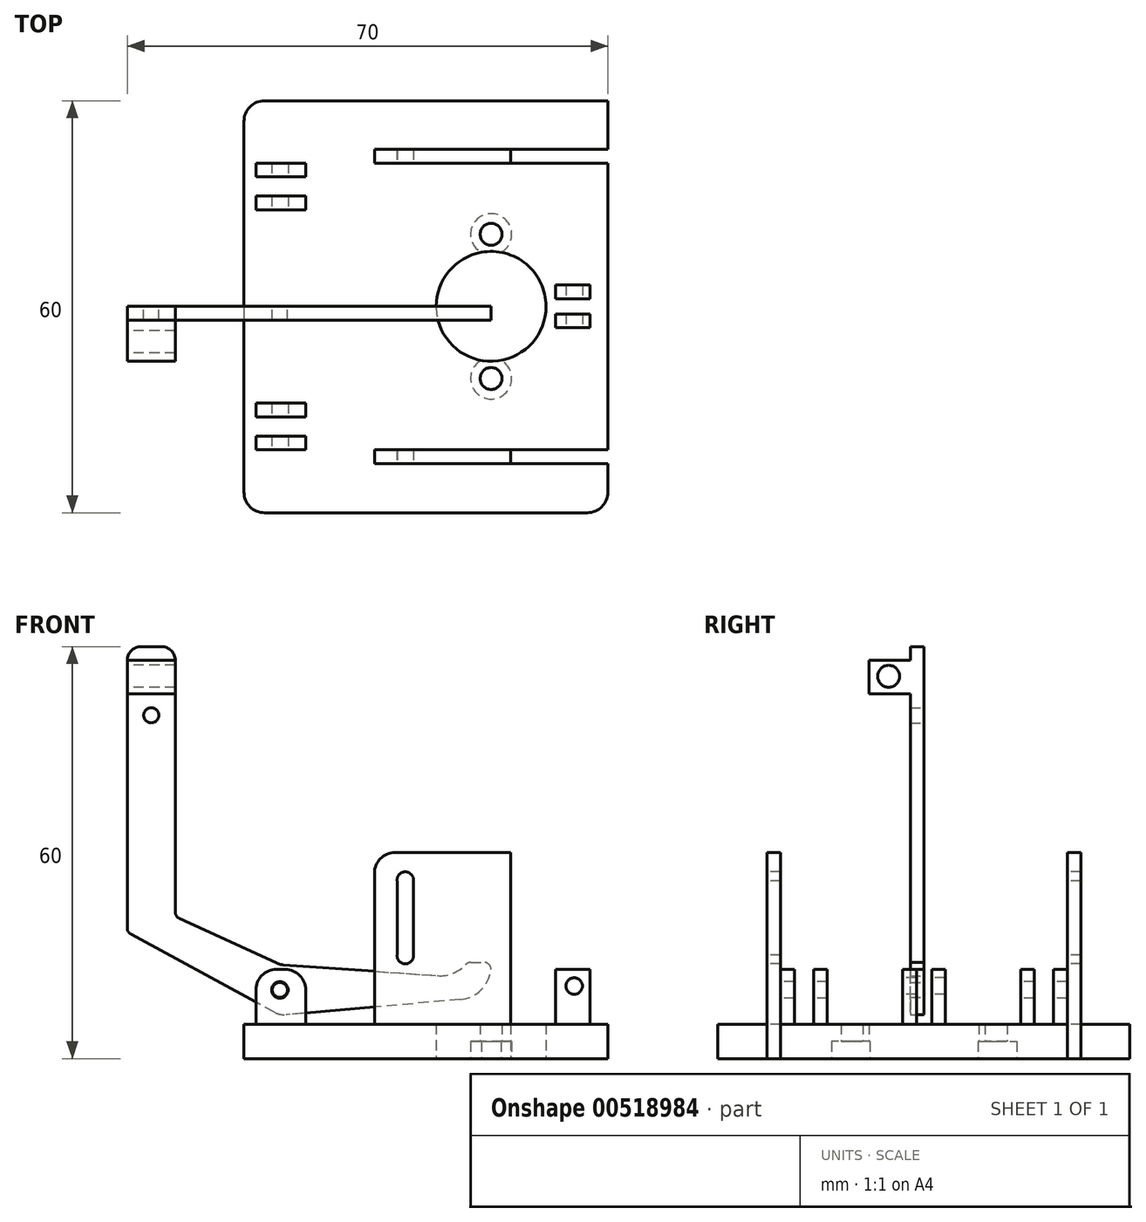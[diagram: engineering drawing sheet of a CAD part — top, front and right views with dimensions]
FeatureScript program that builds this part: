
annotation { "Feature Type Name" : "Feature", "Feature Type Description" : "" }
export const myFeature = defineFeature(function(context is Context, id is Id, definition is map)
    precondition{}
    {
        {
            var Q0;
            Q0=qCreatedBy(makeId("Top.planeOp"),FACE);
            var sketch = newSketch(context, id + "F0", { "sketchPlane" : qUnion([Q0])});
            skLineSegment(sketch, "E0.bottom", {"start": v(-36, 29.94) * mm, "end": v(17, 29.94) * mm});
            skLineSegment(sketch, "E0.top", {"start": v(-36, -30.06) * mm, "end": v(17, -30.06) * mm});
            skLineSegment(sketch, "E0.left", {"start": v(-36, 29.94) * mm, "end": v(-36, -30.06) * mm});
            skLineSegment(sketch, "E0.right", {"start": v(17, 29.94) * mm, "end": v(17, -30.06) * mm});
            skCircle(sketch, "E1.cCircle", {"center": v(0, 22.5) * mm, "radius": 2.85 * mm, "construction": true});
            skLineSegment(sketch, "E1.0", {"start": v(2.85, 20.85) * mm, "end": v(0, 19.2) * mm});
            skLineSegment(sketch, "E1.1", {"start": v(0, 19.2) * mm, "end": v(-2.85, 20.85) * mm});
            skLineSegment(sketch, "E1.2", {"start": v(-2.85, 20.85) * mm, "end": v(-2.85, 24.15) * mm});
            skLineSegment(sketch, "E1.3", {"start": v(-2.85, 24.15) * mm, "end": v(0, 25.8) * mm});
            skLineSegment(sketch, "E1.4", {"start": v(0, 25.8) * mm, "end": v(2.85, 24.15) * mm});
            skLineSegment(sketch, "E1.5", {"start": v(2.85, 24.15) * mm, "end": v(2.85, 20.85) * mm});
            skPoint(sketch, "E1.0.midPoint", {"position": v(1.43, 20.03) * mm});
            skCircle(sketch, "E2.cCircle", {"center": v(0, -22.5) * mm, "radius": 2.85 * mm, "construction": true});
            skLineSegment(sketch, "E2.0", {"start": v(2.85, -24.15) * mm, "end": v(0, -25.8) * mm});
            skLineSegment(sketch, "E2.1", {"start": v(0, -25.8) * mm, "end": v(-2.85, -24.15) * mm});
            skLineSegment(sketch, "E2.2", {"start": v(-2.85, -24.15) * mm, "end": v(-2.85, -20.85) * mm});
            skLineSegment(sketch, "E2.3", {"start": v(-2.85, -20.85) * mm, "end": v(0, -19.2) * mm});
            skLineSegment(sketch, "E2.4", {"start": v(0, -19.2) * mm, "end": v(2.85, -20.85) * mm});
            skLineSegment(sketch, "E2.5", {"start": v(2.85, -20.85) * mm, "end": v(2.85, -24.15) * mm});
            skPoint(sketch, "E2.0.midPoint", {"position": v(1.43, -24.97) * mm});
            skCircle(sketch, "E3", {"center": v(0, 22.5) * mm, "radius": 1.6 * mm});
            skCircle(sketch, "E4", {"center": v(0, -22.5) * mm, "radius": 1.6 * mm});
            skCircle(sketch, "E5", {"center": v(0, 0) * mm, "radius": 8 * mm});
            skLineSegment(sketch, "E6", {"start": v(0, 22.5) * mm, "end": v(0, 0) * mm, "construction": true});
            skLineSegment(sketch, "E7", {"start": v(0, 0) * mm, "end": v(0, -22.5) * mm, "construction": true});
            skCircle(sketch, "E8", {"center": v(0, 10.5) * mm, "radius": 3 * mm});
            skCircle(sketch, "E9", {"center": v(0, -10.5) * mm, "radius": 3 * mm});
            skPoint(sketch, "E10", {"position": v(0, 11.25) * mm});
            skCircle(sketch, "E11", {"center": v(0, 10.5) * mm, "radius": 1.6 * mm});
            skCircle(sketch, "E12", {"center": v(0, -10.5) * mm, "radius": 1.6 * mm});
            skLineSegment(sketch, "E13.bottom", {"start": v(17, 20.85) * mm, "end": v(-17, 20.85) * mm});
            skLineSegment(sketch, "E13.top", {"start": v(17, 22.85) * mm, "end": v(-17, 22.85) * mm});
            skLineSegment(sketch, "E13.left", {"start": v(17, 20.85) * mm, "end": v(17, 22.85) * mm});
            skLineSegment(sketch, "E13.right", {"start": v(-17, 20.85) * mm, "end": v(-17, 22.85) * mm});
            skLineSegment(sketch, "E14.bottom", {"start": v(17, -22.9) * mm, "end": v(-17, -22.9) * mm});
            skLineSegment(sketch, "E14.top", {"start": v(17, -20.9) * mm, "end": v(-17, -20.9) * mm});
            skLineSegment(sketch, "E14.left", {"start": v(17, -22.9) * mm, "end": v(17, -20.9) * mm});
            skLineSegment(sketch, "E14.right", {"start": v(-17, -22.9) * mm, "end": v(-17, -20.9) * mm});
            skLineSegment(sketch, "E15", {"start": v(0, 0) * mm, "end": v(17, -0.06) * mm, "construction": true});
            skLineSegment(sketch, "E16", {"start": v(5.66, -0.02) * mm, "end": v(5.73, 20.85) * mm, "construction": true});
            skLineSegment(sketch, "E17", {"start": v(5.66, -0.02) * mm, "end": v(5.66, -20.9) * mm, "construction": true});
            skLineSegment(sketch, "E18", {"start": v(0, -22.5) * mm, "end": v(17, -22.5) * mm, "construction": true});
            skLineSegment(sketch, "E19", {"start": v(0, -22.5) * mm, "end": v(-17, -22.5) * mm, "construction": true});
            skSolve(sketch);
        }
        {
            var Q0;
            Q0=makeQuery(id+"F0.imprint","IMPRINT",FACE,{"disambiguationData":[TD([[makeQuery(id+"F0.imprint","IMPRINT",EDGE,{"derivedFrom":sQuery(id+"F0.wireOp",EDGE,"E0.bottom")}),-1.0]])]});
            var Q1;
            Q1=makeQuery(id+"F0.imprint","IMPRINT",FACE,{"disambiguationData":[TD([[makeQuery(id+"F0.imprint","IMPRINT",EDGE,{"derivedFrom":sQuery(id+"F0.wireOp",EDGE,"E1.0")}),-1.0]])]});
            var Q2;
            Q2=makeQuery(id+"F0.imprint","IMPRINT",FACE,{"disambiguationData":[TD([[makeQuery(id+"F0.imprint","IMPRINT",EDGE,{"derivedFrom":sQuery(id+"F0.wireOp",EDGE,"E11")}),-1.0]])]});
            var Q3;
            Q3=makeQuery(id+"F0.imprint","IMPRINT",FACE,{"disambiguationData":[TD([[makeQuery(id+"F0.imprint","IMPRINT",EDGE,{"derivedFrom":sQuery(id+"F0.wireOp",EDGE,"E12")}),-1.0]])]});
            var Q4;
            {var subQ5=sQuery(id+"F0.wireOp",EDGE,"E13.right");Q4=makeQuery(id+"F0.imprint","IMPRINT",FACE,{"disambiguationData":[TD([[makeQuery(id+"F0.imprint","IMPRINT",EDGE,{"derivedFrom":subQ5}),-1.0]])]});}
            var Q5;
            {var subQ5=sQuery(id+"F0.wireOp",EDGE,"E13.left");Q5=makeQuery(id+"F0.imprint","IMPRINT",FACE,{"disambiguationData":[TD([[makeQuery(id+"F0.imprint","IMPRINT",EDGE,{"derivedFrom":subQ5}),1.0]])]});}
            var Q6;
            {var subQ5=sQuery(id+"F0.wireOp",EDGE,"E13.top");var subQ6=sQuery(id+"F0.wireOp",EDGE,"E3");var subQ7=makeQuery(id+"F0.imprint","INTERSECT",VERTEX,{"disambiguationData":[OD(0.0)],"derivedFrom":[subQ6,subQ5]});Q6=makeQuery(id+"F0.imprint","IMPRINT",FACE,{"disambiguationData":[TD([[makeQuery(id+"F0.imprint","IMPRINT",EDGE,{"disambiguationData":[TD([[subQ7,1.0]])],"derivedFrom":subQ6}),-1.0]])]});}
            var Q7;
            {var subQ0=sQuery(id+"F0.wireOp",EDGE,"E13.top");var subQ1=sQuery(id+"F0.wireOp",EDGE,"E3");var subQ2=makeQuery(id+"F0.imprint","INTERSECT",VERTEX,{"disambiguationData":[OD(0.0)],"derivedFrom":[subQ1,subQ0]});Q7=makeQuery(id+"F0.imprint","IMPRINT",FACE,{"disambiguationData":[TD([[makeQuery(id+"F0.imprint","IMPRINT",EDGE,{"disambiguationData":[TD([[subQ2,1.0]])],"derivedFrom":subQ1}),1.0]])]});}
            var Q8;
            {var subQ5=sQuery(id+"F0.wireOp",EDGE,"E14.right");Q8=makeQuery(id+"F0.imprint","IMPRINT",FACE,{"disambiguationData":[TD([[makeQuery(id+"F0.imprint","IMPRINT",EDGE,{"derivedFrom":subQ5}),-1.0]])]});}
            var Q9;
            {var subQ0=sQuery(id+"F0.wireOp",EDGE,"E14.bottom");var subQ8=sQuery(id+"F0.wireOp",EDGE,"E2.2");var subQ9=makeQuery(id+"F0.imprint","INTERSECT",VERTEX,{"derivedFrom":[subQ8,subQ0]});Q9=makeQuery(id+"F0.imprint","IMPRINT",FACE,{"disambiguationData":[TD([[makeQuery(id+"F0.imprint","IMPRINT",EDGE,{"disambiguationData":[TD([[subQ9,-1.0]])],"derivedFrom":subQ8}),-1.0]])]});}
            var Q10;
            {var subQ0=sQuery(id+"F0.wireOp",EDGE,"E14.bottom");var subQ1=sQuery(id+"F0.wireOp",EDGE,"E4");var subQ2=makeQuery(id+"F0.imprint","INTERSECT",VERTEX,{"disambiguationData":[OD(0.0)],"derivedFrom":[subQ1,subQ0]});Q10=makeQuery(id+"F0.imprint","IMPRINT",FACE,{"disambiguationData":[TD([[makeQuery(id+"F0.imprint","IMPRINT",EDGE,{"disambiguationData":[TD([[subQ2,-1.0]])],"derivedFrom":subQ1}),1.0]])]});}
            var Q11;
            {var subQ6=sQuery(id+"F0.wireOp",EDGE,"E2.3");Q11=makeQuery(id+"F0.imprint","IMPRINT",FACE,{"disambiguationData":[TD([[makeQuery(id+"F0.imprint","IMPRINT",EDGE,{"derivedFrom":subQ6}),-1.0]])]});}
            var Q12;
            {var subQ5=sQuery(id+"F0.wireOp",EDGE,"E14.left");Q12=makeQuery(id+"F0.imprint","IMPRINT",FACE,{"disambiguationData":[TD([[makeQuery(id+"F0.imprint","IMPRINT",EDGE,{"derivedFrom":subQ5}),1.0]])]});}
            var Q13;
            {var subQ0=sQuery(id+"F0.wireOp",EDGE,"E14.bottom");var subQ1=sQuery(id+"F0.wireOp",EDGE,"E4");var subQ2=makeQuery(id+"F0.imprint","INTERSECT",VERTEX,{"disambiguationData":[OD(0.0)],"derivedFrom":[subQ1,subQ0]});Q13=makeQuery(id+"F0.imprint","IMPRINT",FACE,{"disambiguationData":[TD([[makeQuery(id+"F0.imprint","IMPRINT",EDGE,{"disambiguationData":[TD([[subQ2,1.0]])],"derivedFrom":subQ1}),1.0]])]});}
            var Q14;
            {var subQ8=sQuery(id+"F0.wireOp",EDGE,"E1.3");Q14=makeQuery(id+"F0.imprint","IMPRINT",FACE,{"disambiguationData":[TD([[makeQuery(id+"F0.imprint","IMPRINT",EDGE,{"derivedFrom":subQ8}),-1.0]])]});}
            var Q15;
            {var subQ0=sQuery(id+"F0.wireOp",EDGE,"E13.top");var subQ1=sQuery(id+"F0.wireOp",EDGE,"E3");var subQ2=makeQuery(id+"F0.imprint","INTERSECT",VERTEX,{"disambiguationData":[OD(0.0)],"derivedFrom":[subQ1,subQ0]});Q15=makeQuery(id+"F0.imprint","IMPRINT",FACE,{"disambiguationData":[TD([[makeQuery(id+"F0.imprint","IMPRINT",EDGE,{"disambiguationData":[TD([[subQ2,-1.0]])],"derivedFrom":subQ1}),1.0]])]});}
            var Q16;
            {var subQ1=sQuery(id+"F0.wireOp",EDGE,"E2.0");Q16=makeQuery(id+"F0.imprint","IMPRINT",FACE,{"disambiguationData":[TD([[makeQuery(id+"F0.imprint","IMPRINT",EDGE,{"derivedFrom":subQ1}),-1.0]])]});}
            extrude(context, id + "F1", {"entities" : qUnion([Q0, Q1, Q2, Q3, Q4, Q5, Q6, Q7, Q8, Q9, Q10, Q11, Q12, Q13, Q14, Q15, Q16]), "depth" : 5 * mm, "offsetDistance" : 25 * mm});
        }
        {
            var Q0;
            Q0=makeQuery(id+"F0.imprint","IMPRINT",FACE,{"disambiguationData":[TD([[makeQuery(id+"F0.imprint","IMPRINT",EDGE,{"derivedFrom":sQuery(id+"F0.wireOp",EDGE,"E11")}),-1.0]])]});
            var Q1;
            Q1=makeQuery(id+"F0.imprint","IMPRINT",FACE,{"disambiguationData":[TD([[makeQuery(id+"F0.imprint","IMPRINT",EDGE,{"derivedFrom":sQuery(id+"F0.wireOp",EDGE,"E12")}),-1.0]])]});
            extrude(context, id + "F2", {"entities" : qUnion([Q0, Q1]), "operationType" : NewBodyOperationType.REMOVE, "depth" : 2.5 * mm, "offsetDistance" : 25 * mm});
        }
        {
            var Q0;
            {var subQ5=sQuery(id+"F0.wireOp",EDGE,"E14.right");Q0=makeQuery(id+"F0.imprint","IMPRINT",FACE,{"disambiguationData":[TD([[makeQuery(id+"F0.imprint","IMPRINT",EDGE,{"derivedFrom":subQ5}),-1.0]])]});}
            var Q1;
            {var subQ0=sQuery(id+"F0.wireOp",EDGE,"E14.bottom");var subQ8=sQuery(id+"F0.wireOp",EDGE,"E2.2");var subQ9=makeQuery(id+"F0.imprint","INTERSECT",VERTEX,{"derivedFrom":[subQ8,subQ0]});Q1=makeQuery(id+"F0.imprint","IMPRINT",FACE,{"disambiguationData":[TD([[makeQuery(id+"F0.imprint","IMPRINT",EDGE,{"disambiguationData":[TD([[subQ9,-1.0]])],"derivedFrom":subQ8}),-1.0]])]});}
            var Q2;
            {var subQ0=sQuery(id+"F0.wireOp",EDGE,"E14.bottom");var subQ1=sQuery(id+"F0.wireOp",EDGE,"E4");var subQ2=makeQuery(id+"F0.imprint","INTERSECT",VERTEX,{"disambiguationData":[OD(0.0)],"derivedFrom":[subQ1,subQ0]});Q2=makeQuery(id+"F0.imprint","IMPRINT",FACE,{"disambiguationData":[TD([[makeQuery(id+"F0.imprint","IMPRINT",EDGE,{"disambiguationData":[TD([[subQ2,-1.0]])],"derivedFrom":subQ1}),1.0]])]});}
            var Q3;
            {var subQ5=sQuery(id+"F0.wireOp",EDGE,"E14.left");Q3=makeQuery(id+"F0.imprint","IMPRINT",FACE,{"disambiguationData":[TD([[makeQuery(id+"F0.imprint","IMPRINT",EDGE,{"derivedFrom":subQ5}),1.0]])]});}
            var Q4;
            {var subQ5=sQuery(id+"F0.wireOp",EDGE,"E13.right");Q4=makeQuery(id+"F0.imprint","IMPRINT",FACE,{"disambiguationData":[TD([[makeQuery(id+"F0.imprint","IMPRINT",EDGE,{"derivedFrom":subQ5}),-1.0]])]});}
            var Q5;
            {var subQ5=sQuery(id+"F0.wireOp",EDGE,"E13.top");var subQ6=sQuery(id+"F0.wireOp",EDGE,"E3");var subQ7=makeQuery(id+"F0.imprint","INTERSECT",VERTEX,{"disambiguationData":[OD(0.0)],"derivedFrom":[subQ6,subQ5]});Q5=makeQuery(id+"F0.imprint","IMPRINT",FACE,{"disambiguationData":[TD([[makeQuery(id+"F0.imprint","IMPRINT",EDGE,{"disambiguationData":[TD([[subQ7,1.0]])],"derivedFrom":subQ6}),-1.0]])]});}
            var Q6;
            {var subQ0=sQuery(id+"F0.wireOp",EDGE,"E13.top");var subQ1=sQuery(id+"F0.wireOp",EDGE,"E3");var subQ2=makeQuery(id+"F0.imprint","INTERSECT",VERTEX,{"disambiguationData":[OD(0.0)],"derivedFrom":[subQ1,subQ0]});Q6=makeQuery(id+"F0.imprint","IMPRINT",FACE,{"disambiguationData":[TD([[makeQuery(id+"F0.imprint","IMPRINT",EDGE,{"disambiguationData":[TD([[subQ2,1.0]])],"derivedFrom":subQ1}),1.0]])]});}
            var Q7;
            {var subQ5=sQuery(id+"F0.wireOp",EDGE,"E13.left");Q7=makeQuery(id+"F0.imprint","IMPRINT",FACE,{"disambiguationData":[TD([[makeQuery(id+"F0.imprint","IMPRINT",EDGE,{"derivedFrom":subQ5}),1.0]])]});}
            extrude(context, id + "F3", {"entities" : qUnion([Q0, Q1, Q2, Q3, Q4, Q5, Q6, Q7]), "operationType" : NewBodyOperationType.ADD, "depth" : 30 * mm, "offsetDistance" : 25 * mm});
        }
        {
            var Q0;
            Q0=makeQuery(id+"F3.opExtrude","SWEPT_FACE",FACE,{"disambiguationData":[OSD([sQuery(id+"F0.wireOp",EDGE,"E14.bottom")])]});
            var sketch = newSketch(context, id + "F4", { "sketchPlane" : qUnion([Q0])});
            skCircle(sketch, "E20", {"center": v(-12.5, 26) * mm, "radius": 1.2 * mm});
            skCircle(sketch, "E21", {"center": v(-12.5, 15) * mm, "radius": 1.2 * mm});
            skCircle(sketch, "E22", {"center": v(12.5, 15) * mm, "radius": 1.2 * mm});
            skCircle(sketch, "E23", {"center": v(12.5, 26) * mm, "radius": 1.2 * mm});
            skLineSegment(sketch, "E24", {"start": v(-13.7, 25.89) * mm, "end": v(-13.7, 14.89) * mm});
            skLineSegment(sketch, "E25", {"start": v(-13.7, 14.89) * mm, "end": v(-11.3, 14.89) * mm});
            skLineSegment(sketch, "E26", {"start": v(-11.3, 14.89) * mm, "end": v(-11.3, 25.89) * mm});
            skLineSegment(sketch, "E27", {"start": v(-11.3, 25.89) * mm, "end": v(-13.7, 25.89) * mm});
            skLineSegment(sketch, "E28", {"start": v(11.3, 15.05) * mm, "end": v(11.3, 26) * mm});
            skLineSegment(sketch, "E29", {"start": v(13.67, 26.28) * mm, "end": v(13.7, 15) * mm});
            skLineSegment(sketch, "E30", {"start": v(12.5, 15) * mm, "end": v(17, 15) * mm, "construction": true});
            skLineSegment(sketch, "E31", {"start": v(-12.5, 15) * mm, "end": v(-17, 15) * mm, "construction": true});
            skSolve(sketch);
        }
        {
            var Q0;
            Q0=qSketchRegion(id+"F4",true);
            extrude(context, id + "F5", {"entities" : qUnion([Q0]), "operationType" : NewBodyOperationType.REMOVE, "oppositeDirection" : true, "depth" : 60 * mm, "offsetDistance" : 25 * mm});
        }
        {
            var Q0;
            Q0=makeQuery(id+"F1.opExtrude","CAP_FACE",FACE,{"disambiguationData":[OSD([sQuery(id+"F0.wireOp",EDGE,"E0.bottom"),sQuery(id+"F0.wireOp",EDGE,"E0.top"),sQuery(id+"F0.wireOp",EDGE,"E0.left"),sQuery(id+"F0.wireOp",EDGE,"E0.right"),sQuery(id+"F0.wireOp",EDGE,"E5"),sQuery(id+"F0.wireOp",EDGE,"E11"),sQuery(id+"F0.wireOp",EDGE,"E12")])],"isStart":false});
            var sketch = newSketch(context, id + "F6", { "sketchPlane" : qUnion([Q0])});
            skLineSegment(sketch, "E32.bottom", {"start": v(-27, 20.85) * mm, "end": v(-34.26, 20.85) * mm});
            skLineSegment(sketch, "E32.top", {"start": v(-27, 18.85) * mm, "end": v(-34.26, 18.85) * mm});
            skLineSegment(sketch, "E32.left", {"start": v(-27, 20.85) * mm, "end": v(-27, 18.85) * mm});
            skLineSegment(sketch, "E32.right", {"start": v(-34.26, 20.85) * mm, "end": v(-34.26, 18.85) * mm});
            skLineSegment(sketch, "E33.bottom", {"start": v(-27, 16.05) * mm, "end": v(-34.26, 16.05) * mm});
            skLineSegment(sketch, "E33.top", {"start": v(-27, 14.05) * mm, "end": v(-34.26, 14.05) * mm});
            skLineSegment(sketch, "E33.left", {"start": v(-27, 16.05) * mm, "end": v(-27, 14.05) * mm});
            skLineSegment(sketch, "E33.right", {"start": v(-34.26, 16.05) * mm, "end": v(-34.26, 14.05) * mm});
            skLineSegment(sketch, "E34.bottom", {"start": v(-34.26, -14.1) * mm, "end": v(-27, -14.1) * mm});
            skLineSegment(sketch, "E34.top", {"start": v(-34.26, -16.1) * mm, "end": v(-27, -16.1) * mm});
            skLineSegment(sketch, "E34.left", {"start": v(-34.26, -14.1) * mm, "end": v(-34.26, -16.1) * mm});
            skLineSegment(sketch, "E34.right", {"start": v(-27, -14.1) * mm, "end": v(-27, -16.1) * mm});
            skLineSegment(sketch, "E35.bottom", {"start": v(-27, -18.9) * mm, "end": v(-34.26, -18.9) * mm});
            skLineSegment(sketch, "E35.top", {"start": v(-27, -20.9) * mm, "end": v(-34.26, -20.9) * mm});
            skLineSegment(sketch, "E35.left", {"start": v(-27, -18.9) * mm, "end": v(-27, -20.9) * mm});
            skLineSegment(sketch, "E35.right", {"start": v(-34.26, -18.9) * mm, "end": v(-34.26, -20.9) * mm});
            skLineSegment(sketch, "E36", {"start": v(-34.26, -16.1) * mm, "end": v(-34.26, -18.9) * mm, "construction": true});
            skLineSegment(sketch, "E37", {"start": v(-34.26, 18.85) * mm, "end": v(-34.26, 16.05) * mm, "construction": true});
            skLineSegment(sketch, "E38.bottom", {"start": v(9.37, 3.1) * mm, "end": v(14.37, 3.1) * mm});
            skLineSegment(sketch, "E38.top", {"start": v(9.37, 1.1) * mm, "end": v(14.37, 1.1) * mm});
            skLineSegment(sketch, "E38.left", {"start": v(9.37, 3.1) * mm, "end": v(9.37, 1.1) * mm});
            skLineSegment(sketch, "E38.right", {"start": v(14.37, 3.1) * mm, "end": v(14.37, 1.1) * mm});
            skLineSegment(sketch, "E39.bottom", {"start": v(9.37, -1.1) * mm, "end": v(14.37, -1.1) * mm});
            skLineSegment(sketch, "E39.top", {"start": v(9.37, -3.1) * mm, "end": v(14.37, -3.1) * mm});
            skLineSegment(sketch, "E39.left", {"start": v(9.37, -1.1) * mm, "end": v(9.37, -3.1) * mm});
            skLineSegment(sketch, "E39.right", {"start": v(14.37, -1.1) * mm, "end": v(14.37, -3.1) * mm});
            skSolve(sketch);
        }
        {
            var Q0;
            Q0=makeQuery(id+"F6.imprint","IMPRINT",FACE,{"disambiguationData":[TD([[makeQuery(id+"F6.imprint","IMPRINT",EDGE,{"derivedFrom":sQuery(id+"F6.wireOp",EDGE,"E32.bottom")}),1.0]])]});
            var Q1;
            Q1=makeQuery(id+"F6.imprint","IMPRINT",FACE,{"disambiguationData":[TD([[makeQuery(id+"F6.imprint","IMPRINT",EDGE,{"derivedFrom":sQuery(id+"F6.wireOp",EDGE,"E33.bottom")}),1.0]])]});
            var Q2;
            Q2=makeQuery(id+"F6.imprint","IMPRINT",FACE,{"disambiguationData":[TD([[makeQuery(id+"F6.imprint","IMPRINT",EDGE,{"derivedFrom":sQuery(id+"F6.wireOp",EDGE,"E34.bottom")}),-1.0]])]});
            var Q3;
            Q3=makeQuery(id+"F6.imprint","IMPRINT",FACE,{"disambiguationData":[TD([[makeQuery(id+"F6.imprint","IMPRINT",EDGE,{"derivedFrom":sQuery(id+"F6.wireOp",EDGE,"E35.bottom")}),1.0]])]});
            var Q4;
            Q4=makeQuery(id+"F6.imprint","IMPRINT",FACE,{"disambiguationData":[TD([[makeQuery(id+"F6.imprint","IMPRINT",EDGE,{"derivedFrom":sQuery(id+"F6.wireOp",EDGE,"E38.bottom")}),-1.0]])]});
            var Q5;
            Q5=makeQuery(id+"F6.imprint","IMPRINT",FACE,{"disambiguationData":[TD([[makeQuery(id+"F6.imprint","IMPRINT",EDGE,{"derivedFrom":sQuery(id+"F6.wireOp",EDGE,"E39.bottom")}),-1.0]])]});
            extrude(context, id + "F7", {"entities" : qUnion([Q0, Q1, Q2, Q3, Q4, Q5]), "operationType" : NewBodyOperationType.ADD, "depth" : 8 * mm, "offsetDistance" : 25 * mm});
        }
        {
            var Q0;
            Q0=makeQuery(id+"F7.opExtrude","SWEPT_FACE",FACE,{"disambiguationData":[OSD([sQuery(id+"F6.wireOp",EDGE,"E35.top")])]});
            var sketch = newSketch(context, id + "F8", { "sketchPlane" : qUnion([Q0])});
            skCircle(sketch, "E40", {"center": v(-30.76, 10) * mm, "radius": 1.2 * mm});
            skCircle(sketch, "E41", {"center": v(12.1, 10.57) * mm, "radius": 1.2 * mm});
            skSolve(sketch);
        }
        {
            var Q0;
            Q0=makeQuery(id+"F8.imprint","IMPRINT",FACE,{"disambiguationData":[TD([[makeQuery(id+"F8.imprint","IMPRINT",EDGE,{"derivedFrom":sQuery(id+"F8.wireOp",EDGE,"E40")}),1.0]])]});
            var Q1;
            Q1=makeQuery(id+"F8.imprint","IMPRINT",FACE,{"disambiguationData":[TD([[makeQuery(id+"F8.imprint","IMPRINT",EDGE,{"derivedFrom":sQuery(id+"F8.wireOp",EDGE,"E41")}),1.0]])]});
            extrude(context, id + "F9", {"entities" : qUnion([Q0, Q1]), "operationType" : NewBodyOperationType.REMOVE, "oppositeDirection" : true, "depth" : 60 * mm, "offsetDistance" : 25 * mm});
        }
        {
            var Q0;
            Q0=qCreatedBy(makeId("Front.planeOp"),FACE);
            var sketch = newSketch(context, id + "F10", { "sketchPlane" : qUnion([Q0])});
            skLineSegment(sketch, "E42", {"start": v(0, 9) * mm, "end": v(-29.86, 6.4) * mm});
            skLineSegment(sketch, "E43", {"start": v(-31.56, 6.74) * mm, "end": v(-53, 18.4) * mm});
            skLineSegment(sketch, "E44", {"start": v(-53, 18.4) * mm, "end": v(-53, 58) * mm});
            skLineSegment(sketch, "E45", {"start": v(-51, 60) * mm, "end": v(-48, 60) * mm});
            skLineSegment(sketch, "E46", {"start": v(-46, 58) * mm, "end": v(-46, 20.68) * mm});
            skLineSegment(sketch, "E47", {"start": v(-46, 20.68) * mm, "end": v(-31.26, 13.91) * mm});
            skLineSegment(sketch, "E48", {"start": v(-30.22, 13.65) * mm, "end": v(-4, 11.81) * mm});
            skLineSegment(sketch, "E49", {"start": v(-4, 11.81) * mm, "end": v(-4, 14) * mm});
            skLineSegment(sketch, "E50", {"start": v(-4, 14) * mm, "end": v(0, 14) * mm});
            skLineSegment(sketch, "E51", {"start": v(0, 9) * mm, "end": v(0, 14) * mm});
            skCircle(sketch, "E52", {"center": v(-30.76, 10) * mm, "radius": 1.1 * mm});
            skPoint(sketch, "E53.visualSharp", {"position": v(-46, 60) * mm});
            skArc(sketch, "E53.filletArc", {"start": v(-46, 58) * mm, "mid": v(-46.59, 59.41) * mm, "end": v(-48, 60) * mm});
            skPoint(sketch, "E54.visualSharp", {"position": v(-53, 60) * mm});
            skArc(sketch, "E54.filletArc", {"start": v(-51, 60) * mm, "mid": v(-52.41, 59.41) * mm, "end": v(-53, 58) * mm});
            skCircle(sketch, "E55", {"center": v(-49.5, 50) * mm, "radius": 1.1 * mm});
            skPoint(sketch, "E55.centerSnap0", {"position": v(-49.5, 60) * mm});
            skLineSegment(sketch, "E56", {"start": v(-30.76, 10) * mm, "end": v(-30.76, 13.69) * mm, "construction": true});
            skLineSegment(sketch, "E57", {"start": v(-30.76, 10) * mm, "end": v(-30.76, 6.31) * mm, "construction": true});
            skPoint(sketch, "E58.visualSharp", {"position": v(-30.76, 6.31) * mm});
            skArc(sketch, "E58.filletArc", {"start": v(-31.56, 6.74) * mm, "mid": v(-30.74, 6.44) * mm, "end": v(-29.86, 6.4) * mm});
            skPoint(sketch, "E59.visualSharp", {"position": v(-30.76, 13.69) * mm});
            skArc(sketch, "E59.filletArc", {"start": v(-31.26, 13.91) * mm, "mid": v(-30.75, 13.73) * mm, "end": v(-30.22, 13.65) * mm});
            skLineSegment(sketch, "E60", {"start": v(-53, 53.14) * mm, "end": v(-46, 53.14) * mm});
            skLineSegment(sketch, "E61", {"start": v(-46, 53.14) * mm, "end": v(-46, 58) * mm});
            skLineSegment(sketch, "E62", {"start": v(-53, 58) * mm, "end": v(-53, 53.14) * mm});
            skLineSegment(sketch, "E63", {"start": v(-53, 58) * mm, "end": v(-46, 58) * mm});
            skSolve(sketch);
        }
        {
            var Q0;
            Q0=makeQuery(id+"F10.imprint","IMPRINT",FACE,{"disambiguationData":[TD([[makeQuery(id+"F10.imprint","IMPRINT",EDGE,{"derivedFrom":sQuery(id+"F10.wireOp",EDGE,"E42")}),-1.0]])]});
            var Q1;
            Q1=makeQuery(id+"F10.imprint","IMPRINT",FACE,{"disambiguationData":[TD([[makeQuery(id+"F10.imprint","IMPRINT",EDGE,{"derivedFrom":sQuery(id+"F10.wireOp",EDGE,"E45")}),-1.0]])]});
            var Q2;
            Q2=makeQuery(id+"F10.imprint","IMPRINT",FACE,{"disambiguationData":[TD([[makeQuery(id+"F10.imprint","IMPRINT",EDGE,{"derivedFrom":sQuery(id+"F10.wireOp",EDGE,"E60")}),1.0]])]});
            extrude(context, id + "F11", {"entities" : qUnion([Q0, Q1, Q2]), "depth" : 2 * mm, "offsetDistance" : 25 * mm});
        }
        {
            var Q0;
            Q0=makeQuery(id+"F11.opExtrude","SWEPT_EDGE",EDGE,{"disambiguationData":[OSD([sQuery(id+"F10.wireOp",EDGE,"E45"),sQuery(id+"F10.wireOp",EDGE,"E46")])]});
            var Q1;
            Q1=makeQuery(id+"F11.opExtrude","SWEPT_EDGE",EDGE,{"disambiguationData":[OSD([sQuery(id+"F10.wireOp",EDGE,"E44"),sQuery(id+"F10.wireOp",EDGE,"E45")])]});
            var Q2;
            Q2=makeQuery(id+"F11.opExtrude","SWEPT_EDGE",EDGE,{"disambiguationData":[OSD([sQuery(id+"F10.wireOp",EDGE,"E49"),sQuery(id+"F10.wireOp",EDGE,"E50")])]});
            var Q3;
            Q3=makeQuery(id+"F11.opExtrude","SWEPT_EDGE",EDGE,{"disambiguationData":[OSD([sQuery(id+"F10.wireOp",EDGE,"E50"),sQuery(id+"F10.wireOp",EDGE,"E51")])]});
            fillet(context, id + "F12", {"entities" : qUnion([Q0, Q1, Q2, Q3]), "radius" : 1 * mm, "tangentPropagation" : true, "allowEdgeOverflow" : false});
        }
        {
            var Q0;
            Q0=makeQuery(id+"F11.opExtrude","SWEPT_EDGE",EDGE,{"disambiguationData":[OSD([sQuery(id+"F10.wireOp",EDGE,"E43"),sQuery(id+"F10.wireOp",EDGE,"E44")])]});
            var Q1;
            Q1=makeQuery(id+"F11.opExtrude","SWEPT_EDGE",EDGE,{"disambiguationData":[OSD([sQuery(id+"F10.wireOp",EDGE,"E42"),sQuery(id+"F10.wireOp",EDGE,"E43")])]});
            var Q2;
            Q2=makeQuery(id+"F11.opExtrude","SWEPT_EDGE",EDGE,{"disambiguationData":[OSD([sQuery(id+"F10.wireOp",EDGE,"E47"),sQuery(id+"F10.wireOp",EDGE,"E48")])]});
            fillet(context, id + "F13", {"entities" : qUnion([Q0, Q1, Q2]), "radius" : 5 * mm, "tangentPropagation" : true, "allowEdgeOverflow" : false});
        }
        {
            var Q0;
            Q0=makeQuery(id+"F7.opExtrude","CAP_EDGE",EDGE,{"disambiguationData":[OSD([sQuery(id+"F6.wireOp",EDGE,"E33.right")])],"isStart":false});
            var Q1;
            Q1=makeQuery(id+"F7.opExtrude","CAP_EDGE",EDGE,{"disambiguationData":[OSD([sQuery(id+"F6.wireOp",EDGE,"E32.right")])],"isStart":false});
            var Q2;
            Q2=makeQuery(id+"F7.opExtrude","CAP_EDGE",EDGE,{"disambiguationData":[OSD([sQuery(id+"F6.wireOp",EDGE,"E35.left")])],"isStart":false});
            var Q3;
            Q3=makeQuery(id+"F7.opExtrude","CAP_EDGE",EDGE,{"disambiguationData":[OSD([sQuery(id+"F6.wireOp",EDGE,"E35.right")])],"isStart":false});
            var Q4;
            Q4=makeQuery(id+"F7.opExtrude","CAP_EDGE",EDGE,{"disambiguationData":[OSD([sQuery(id+"F6.wireOp",EDGE,"E34.left")])],"isStart":false});
            var Q5;
            Q5=makeQuery(id+"F7.opExtrude","CAP_EDGE",EDGE,{"disambiguationData":[OSD([sQuery(id+"F6.wireOp",EDGE,"E34.right")])],"isStart":false});
            var Q6;
            Q6=makeQuery(id+"F7.opExtrude","CAP_EDGE",EDGE,{"disambiguationData":[OSD([sQuery(id+"F6.wireOp",EDGE,"E33.left")])],"isStart":false});
            var Q7;
            Q7=makeQuery(id+"F7.opExtrude","CAP_EDGE",EDGE,{"disambiguationData":[OSD([sQuery(id+"F6.wireOp",EDGE,"E32.left")])],"isStart":false});
            var Q8;
            Q8=makeQuery(id+"F3.opExtrude","CAP_EDGE",EDGE,{"disambiguationData":[OSD([sQuery(id+"F0.wireOp",EDGE,"E13.right")])],"isStart":false});
            var Q9;
            Q9=makeQuery(id+"F3.opExtrude","CAP_EDGE",EDGE,{"disambiguationData":[OSD([sQuery(id+"F0.wireOp",EDGE,"E13.left")])],"isStart":false});
            var Q10;
            Q10=makeQuery(id+"F3.opExtrude","CAP_EDGE",EDGE,{"disambiguationData":[OSD([sQuery(id+"F0.wireOp",EDGE,"E14.right")])],"isStart":false});
            var Q11;
            Q11=makeQuery(id+"F3.opExtrude","CAP_EDGE",EDGE,{"disambiguationData":[OSD([sQuery(id+"F0.wireOp",EDGE,"E14.left")])],"isStart":false});
            var Q12;
            Q12=makeQuery(id+"F1.opExtrude","SWEPT_EDGE",EDGE,{"disambiguationData":[OSD([sQuery(id+"F0.wireOp",EDGE,"E0.top"),sQuery(id+"F0.wireOp",EDGE,"E0.right")])]});
            var Q13;
            Q13=makeQuery(id+"F1.opExtrude","SWEPT_EDGE",EDGE,{"disambiguationData":[OSD([sQuery(id+"F0.wireOp",EDGE,"E0.top"),sQuery(id+"F0.wireOp",EDGE,"E0.left")])]});
            var Q14;
            Q14=makeQuery(id+"F1.opExtrude","SWEPT_EDGE",EDGE,{"disambiguationData":[OSD([sQuery(id+"F0.wireOp",EDGE,"E0.bottom"),sQuery(id+"F0.wireOp",EDGE,"E0.left")])]});
            fillet(context, id + "F14", {"entities" : qUnion([Q0, Q1, Q2, Q3, Q4, Q5, Q6, Q7, Q8, Q9, Q10, Q11, Q12, Q13, Q14]), "radius" : 3 * mm, "tangentPropagation" : true, "allowEdgeOverflow" : false});
        }
        {
            var Q0;
            Q0=makeQuery(id+"F10.imprint","IMPRINT",FACE,{"disambiguationData":[TD([[makeQuery(id+"F10.imprint","IMPRINT",EDGE,{"derivedFrom":sQuery(id+"F10.wireOp",EDGE,"E60")}),1.0]])]});
            extrude(context, id + "F15", {"entities" : qUnion([Q0]), "operationType" : NewBodyOperationType.ADD, "depth" : 8 * mm, "offsetDistance" : 25 * mm});
        }
        {
            var Q0;
            {var subQ0=sQuery(id+"F10.wireOp",EDGE,"E62");Q0=makeQuery(id+"F15.boolean.opBoolean","MERGE",FACE,{"derivedFrom":[makeQuery(id+"F11.opExtrude","SWEPT_FACE",FACE,{"disambiguationData":[OSD([sQuery(id+"F10.wireOp",EDGE,"E44"),subQ0])]}),makeQuery(id+"F15.opExtrude","SWEPT_FACE",FACE,{"disambiguationData":[OSD([subQ0])]})]});}
            var sketch = newSketch(context, id + "F16", { "sketchPlane" : qUnion([Q0])});
            skCircle(sketch, "E64", {"center": v(5.16, 55.68) * mm, "radius": 1.6 * mm});
            skSolve(sketch);
        }
        {
            var Q0;
            Q0=makeQuery(id+"F16.imprint","IMPRINT",FACE,{"disambiguationData":[TD([[makeQuery(id+"F16.imprint","IMPRINT",EDGE,{"derivedFrom":sQuery(id+"F16.wireOp",EDGE,"E64")}),1.0]])]});
            extrude(context, id + "F17", {"entities" : qUnion([Q0]), "operationType" : NewBodyOperationType.REMOVE, "oppositeDirection" : true, "depth" : 25 * mm, "offsetDistance" : 25 * mm});
        }
    });
